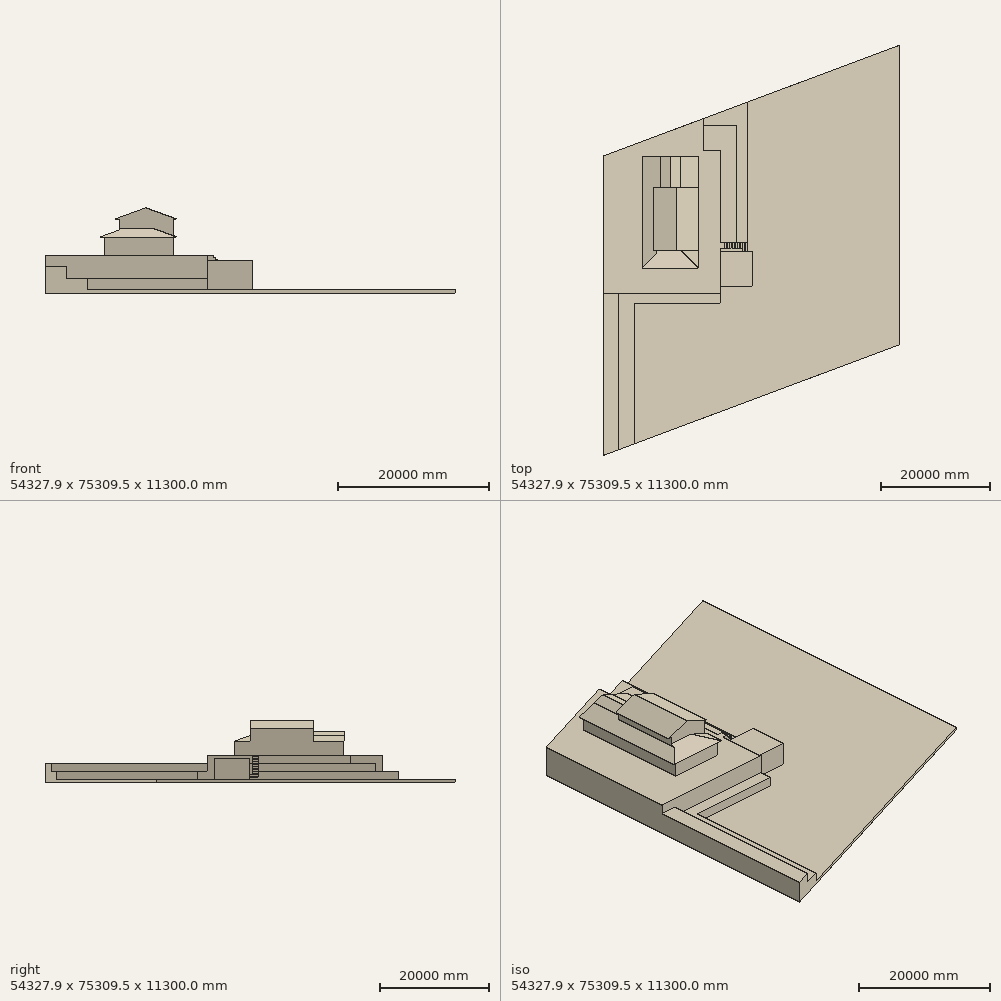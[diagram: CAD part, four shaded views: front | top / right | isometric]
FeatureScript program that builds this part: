
annotation { "Feature Type Name" : "Feature", "Feature Type Description" : "" }
export const myFeature = defineFeature(function(context is Context, id is Id, definition is map)
    precondition{}
    {
        {
            var Q0;
            Q0=qCreatedBy(makeId("Top.planeOp"),FACE);
            var sketch = newSketch(context, id + "F0", { "sketchPlane" : qUnion([Q0])});
            skLineSegment(sketch, "E0.bottom", {"start": v(0, 0) * mm, "end": v(-9140, 0) * mm});
            skLineSegment(sketch, "E0.top", {"start": v(0, 20000) * mm, "end": v(-9140, 20000) * mm});
            skLineSegment(sketch, "E0.left", {"start": v(0, 0) * mm, "end": v(0, 20000) * mm});
            skLineSegment(sketch, "E0.right", {"start": v(-9140, 0) * mm, "end": v(-9140, 20000) * mm});
            skSolve(sketch);
        }
        {
            var Q0;
            Q0 = qSketchRegion(id + "F0", true);
            extrude(context, id + "F1", {"entities" : qUnion([Q0]), "depth" : 2400 * mm, "offsetDistance" : 25 * mm});
        }
        {
            var Q0;
            Q0=makeQuery(id+"F1.opExtrude","CAP_FACE",FACE,{"disambiguationData":[OSD([sQuery(id+"F0.wireOp",EDGE,"E0.bottom"),sQuery(id+"F0.wireOp",EDGE,"E0.top"),sQuery(id+"F0.wireOp",EDGE,"E0.left"),sQuery(id+"F0.wireOp",EDGE,"E0.right")])],"isStart":false});
            var sketch = newSketch(context, id + "F2", { "sketchPlane" : qUnion([Q0])});
            skLineSegment(sketch, "E1", {"start": v(0, 0) * mm, "end": v(0, 3000) * mm});
            skLineSegment(sketch, "E2", {"start": v(0, 3000) * mm, "end": v(-7140, 3000) * mm});
            skLineSegment(sketch, "E3", {"start": v(-7140, 3000) * mm, "end": v(-7140, 14500) * mm});
            skLineSegment(sketch, "E4", {"start": v(-7140, 14500) * mm, "end": v(0, 14500) * mm});
            skLineSegment(sketch, "E5", {"start": v(0, 14500) * mm, "end": v(0, 3000) * mm});
            skSolve(sketch);
        }
        {
            var Q0;
            Q0 = qSketchRegion(id + "F2", true);
            extrude(context, id + "F3", {"entities" : qUnion([Q0]), "operationType" : NewBodyOperationType.ADD, "depth" : 2400 * mm, "offsetDistance" : 25 * mm});
        }
        {
            var Q0;
            Q0=makeQuery(id+"F3.opExtrude","CAP_FACE",FACE,{"disambiguationData":[OSD([sQuery(id+"F2.wireOp",EDGE,"E2"),sQuery(id+"F2.wireOp",EDGE,"E3"),sQuery(id+"F2.wireOp",EDGE,"E4"),sQuery(id+"F2.wireOp",EDGE,"E5")])],"isStart":false});
            var sketch = newSketch(context, id + "F4", { "sketchPlane" : qUnion([Q0])});
            skLineSegment(sketch, "E6", {"start": v(-3570, 3000) * mm, "end": v(-7740, 3000) * mm});
            skLineSegment(sketch, "E7", {"start": v(-7740, 3000) * mm, "end": v(-7740, 14500) * mm});
            skLineSegment(sketch, "E8", {"start": v(-7740, 14500) * mm, "end": v(600, 14500) * mm});
            skLineSegment(sketch, "E9", {"start": v(600, 14500) * mm, "end": v(600, 3000) * mm});
            skLineSegment(sketch, "E10", {"start": v(600, 3000) * mm, "end": v(-3570, 3000) * mm});
            skSolve(sketch);
        }
        {
            var Q0;
            Q0 = qSketchRegion(id + "F4", true);
            extrude(context, id + "F5", {"entities" : qUnion([Q0]), "operationType" : NewBodyOperationType.ADD, "depth" : 1500 * mm, "offsetDistance" : 25 * mm});
        }
        {
            var Q0;
            Q0=makeQuery(id+"F5.opExtrude","CAP_EDGE",EDGE,{"disambiguationData":[OSD([sQuery(id+"F4.wireOp",EDGE,"E9")])],"isStart":false});
            var Q1;
            Q1=makeQuery(id+"F5.opExtrude","CAP_EDGE",EDGE,{"disambiguationData":[OSD([sQuery(id+"F4.wireOp",EDGE,"E7")])],"isStart":false});
            chamfer(context, id + "F6", {"entities" : qUnion([Q0, Q1]), "chamferType" : ChamferType.OFFSET_ANGLE, "width" : 4170 * mm, "oppositeDirection" : true, "angle" : 20 * degree, "tangentPropagation" : true});
        }
        {
            var Q0;
            Q0=makeQuery(id+"F1.opExtrude","CAP_FACE",FACE,{"disambiguationData":[OSD([sQuery(id+"F0.wireOp",EDGE,"E0.bottom"),sQuery(id+"F0.wireOp",EDGE,"E0.top"),sQuery(id+"F0.wireOp",EDGE,"E0.left"),sQuery(id+"F0.wireOp",EDGE,"E0.right")])],"isStart":false});
            var sketch = newSketch(context, id + "F7", { "sketchPlane" : qUnion([Q0])});
            skLineSegment(sketch, "E11", {"start": v(0, 3000) * mm, "end": v(-7140, 3000) * mm});
            skLineSegment(sketch, "E12", {"start": v(-9740, 3000) * mm, "end": v(-9740, -300) * mm});
            skLineSegment(sketch, "E13", {"start": v(-9740, -300) * mm, "end": v(600, -300) * mm});
            skLineSegment(sketch, "E14", {"start": v(600, -300) * mm, "end": v(600, 3000) * mm});
            skLineSegment(sketch, "E15", {"start": v(600, 3000) * mm, "end": v(0, 3000) * mm});
            skPoint(sketch, "E16.start.orphan", {"position": v(600, 14500) * mm});
            skLineSegment(sketch, "E17", {"start": v(-7140, 3000) * mm, "end": v(-7140, 14500) * mm});
            skLineSegment(sketch, "E18", {"start": v(-7140, 14500) * mm, "end": v(600, 14500) * mm});
            skLineSegment(sketch, "E19", {"start": v(600, 14500) * mm, "end": v(600, 20300) * mm});
            skLineSegment(sketch, "E20", {"start": v(600, 20300) * mm, "end": v(-9740, 20300) * mm});
            skLineSegment(sketch, "E21", {"start": v(-9740, 20300) * mm, "end": v(-9740, 3000) * mm});
            skSolve(sketch);
        }
        {
            var Q0;
            Q0 = qSketchRegion(id + "F7", true);
            extrude(context, id + "F8", {"entities" : qUnion([Q0]), "operationType" : NewBodyOperationType.ADD, "depth" : 1200 * mm, "offsetDistance" : 25 * mm});
        }
        {
            var Q0;
            Q0=makeQuery(id+"F8.opExtrude","CAP_EDGE",EDGE,{"disambiguationData":[OSD([sQuery(id+"F7.wireOp",EDGE,"E13")])],"isStart":false});
            var Q1;
            Q1=makeQuery(id+"F8.opExtrude","CAP_EDGE",EDGE,{"disambiguationData":[OSD([sQuery(id+"F7.wireOp",EDGE,"E14")])],"isStart":false});
            chamfer(context, id + "F9", {"entities" : qUnion([Q0, Q1]), "chamferType" : ChamferType.OFFSET_ANGLE, "width" : 3300 * mm, "oppositeDirection" : false, "angle" : 20 * degree, "tangentPropagation" : true});
        }
        {
            var Q0;
            Q0=makeQuery(id+"F8.opExtrude","CAP_EDGE",EDGE,{"disambiguationData":[OSD([sQuery(id+"F7.wireOp",EDGE,"E19")])],"isStart":false});
            var Q1;
            Q1=makeQuery(id+"F8.opExtrude","CAP_EDGE",EDGE,{"disambiguationData":[OSD([sQuery(id+"F7.wireOp",EDGE,"E12"),sQuery(id+"F7.wireOp",EDGE,"E21")])],"isStart":false});
            chamfer(context, id + "F10", {"entities" : qUnion([Q0, Q1]), "chamferType" : ChamferType.OFFSET_ANGLE, "width" : 3300 * mm, "oppositeDirection" : false, "angle" : 20 * degree, "tangentPropagation" : true});
        }
        {
            var Q0;
            Q0=makeQuery(id+"F8.opExtrude","CAP_FACE",FACE,{"disambiguationData":[OSD([sQuery(id+"F7.wireOp",EDGE,"E11"),sQuery(id+"F7.wireOp",EDGE,"E12"),sQuery(id+"F7.wireOp",EDGE,"E13"),sQuery(id+"F7.wireOp",EDGE,"E14"),sQuery(id+"F7.wireOp",EDGE,"E15"),sQuery(id+"F7.wireOp",EDGE,"E17"),sQuery(id+"F7.wireOp",EDGE,"E18"),sQuery(id+"F7.wireOp",EDGE,"E19"),sQuery(id+"F7.wireOp",EDGE,"E20"),sQuery(id+"F7.wireOp",EDGE,"E21")])],"isStart":false});
            extrude(context, id + "F11", {"entities" : qUnion([Q0]), "operationType" : NewBodyOperationType.ADD, "depth" : 700 * mm, "offsetDistance" : 25 * mm});
        }
        {
            var Q0;
            {var subQ0=sQuery(id+"F7.wireOp",EDGE,"E21");var subQ1=sQuery(id+"F7.wireOp",EDGE,"E20");var subQ2=sQuery(id+"F7.wireOp",EDGE,"E19");var subQ3=sQuery(id+"F7.wireOp",EDGE,"E18");var subQ4=sQuery(id+"F7.wireOp",EDGE,"E17");var subQ5=sQuery(id+"F7.wireOp",EDGE,"E15");var subQ6=sQuery(id+"F7.wireOp",EDGE,"E14");var subQ7=sQuery(id+"F7.wireOp",EDGE,"E13");var subQ8=sQuery(id+"F7.wireOp",EDGE,"E12");var subQ9=sQuery(id+"F7.wireOp",EDGE,"E11");Q0=makeQuery(id+"F11.opExtrude","CAP_EDGE",EDGE,{"disambiguationData":[OSD([subQ9,subQ8,subQ7,subQ6,subQ5,subQ4,subQ3,subQ2,subQ1,subQ0]),TDD([makeQuery(id+"F10.opChamfer","BLEND_EDGE",EDGE,{"blendedFrom":[makeQuery(id+"F8.opExtrude","CAP_EDGE",EDGE,{"disambiguationData":[OSD([subQ8,subQ0])],"isStart":false}),makeQuery(id+"F8.opExtrude","CAP_FACE",FACE,{"disambiguationData":[OSD([subQ9,subQ8,subQ7,subQ6,subQ5,subQ4,subQ3,subQ2,subQ1,subQ0])],"isStart":false})],"blendedInto":[makeQuery(id+"F8.opExtrude","CAP_FACE",FACE,{"disambiguationData":[OSD([subQ9,subQ8,subQ7,subQ6,subQ5,subQ4,subQ3,subQ2,subQ1,subQ0])],"isStart":false})]})])],"isStart":false});}
            var Q1;
            {var subQ0=sQuery(id+"F7.wireOp",EDGE,"E21");var subQ1=sQuery(id+"F7.wireOp",EDGE,"E20");var subQ2=sQuery(id+"F7.wireOp",EDGE,"E19");var subQ3=sQuery(id+"F7.wireOp",EDGE,"E18");var subQ4=sQuery(id+"F7.wireOp",EDGE,"E17");var subQ5=sQuery(id+"F7.wireOp",EDGE,"E15");var subQ6=sQuery(id+"F7.wireOp",EDGE,"E14");var subQ7=sQuery(id+"F7.wireOp",EDGE,"E13");var subQ8=sQuery(id+"F7.wireOp",EDGE,"E12");var subQ9=sQuery(id+"F7.wireOp",EDGE,"E11");Q1=makeQuery(id+"F11.opExtrude","CAP_EDGE",EDGE,{"disambiguationData":[OSD([subQ9,subQ8,subQ7,subQ6,subQ5,subQ4,subQ3,subQ2,subQ1,subQ0]),TDD([makeQuery(id+"F10.opChamfer","BLEND_EDGE",EDGE,{"blendedFrom":[makeQuery(id+"F8.opExtrude","CAP_EDGE",EDGE,{"disambiguationData":[OSD([subQ2])],"isStart":false}),makeQuery(id+"F8.opExtrude","CAP_FACE",FACE,{"disambiguationData":[OSD([subQ9,subQ8,subQ7,subQ6,subQ5,subQ4,subQ3,subQ2,subQ1,subQ0])],"isStart":false})],"blendedInto":[makeQuery(id+"F8.opExtrude","CAP_FACE",FACE,{"disambiguationData":[OSD([subQ9,subQ8,subQ7,subQ6,subQ5,subQ4,subQ3,subQ2,subQ1,subQ0])],"isStart":false})]})])],"isStart":false});}
            chamfer(context, id + "F12", {"entities" : qUnion([Q0, Q1]), "chamferType" : ChamferType.OFFSET_ANGLE, "width" : 1923.2 * mm, "oppositeDirection" : false, "angle" : 20 * degree, "tangentPropagation" : true});
        }
        {
            var Q0;
            Q0=makeQuery(id+"F1.opExtrude","CAP_FACE",FACE,{"disambiguationData":[OSD([sQuery(id+"F0.wireOp",EDGE,"E0.bottom"),sQuery(id+"F0.wireOp",EDGE,"E0.top"),sQuery(id+"F0.wireOp",EDGE,"E0.left"),sQuery(id+"F0.wireOp",EDGE,"E0.right")])],"isStart":true});
            var sketch = newSketch(context, id + "F13", { "sketchPlane" : qUnion([Q0])});
            skLineSegment(sketch, "E22", {"start": v(0, 0) * mm, "end": v(0, 3700) * mm});
            skLineSegment(sketch, "E23", {"start": v(0, 3700) * mm, "end": v(4500, 3700) * mm});
            skLineSegment(sketch, "E24", {"start": v(4500, 3700) * mm, "end": v(4500, -28300) * mm});
            skLineSegment(sketch, "E25", {"start": v(0, 3700) * mm, "end": v(-16900, 3700) * mm});
            skLineSegment(sketch, "E26", {"start": v(-16900, 3700) * mm, "end": v(-16900, -20300) * mm});
            skLineSegment(sketch, "E27", {"start": v(-16900, -20300) * mm, "end": v(4500, -28300) * mm});
            skSolve(sketch);
        }
        {
            var Q0;
            Q0 = qSketchRegion(id + "F13", true);
            extrude(context, id + "F14", {"entities" : qUnion([Q0]), "operationType" : NewBodyOperationType.ADD, "depth" : 200 * mm, "offsetDistance" : 25 * mm});
        }
        {
            var Q0;
            Q0=makeQuery(id+"F14.opExtrude","CAP_FACE",FACE,{"disambiguationData":[OSD([sQuery(id+"F13.wireOp",EDGE,"E23"),sQuery(id+"F13.wireOp",EDGE,"E24"),sQuery(id+"F13.wireOp",EDGE,"E25"),sQuery(id+"F13.wireOp",EDGE,"E26"),sQuery(id+"F13.wireOp",EDGE,"E27")])],"isStart":false});
            var sketch = newSketch(context, id + "F15", { "sketchPlane" : qUnion([Q0])});
            skLineSegment(sketch, "E28", {"start": v(-16900, -20300) * mm, "end": v(37427.93, -40609.5) * mm});
            skLineSegment(sketch, "E29", {"start": v(37427.93, -40609.5) * mm, "end": v(37427.93, 14390.5) * mm});
            skLineSegment(sketch, "E30", {"start": v(37427.93, 14390.5) * mm, "end": v(-16900, 34700) * mm});
            skLineSegment(sketch, "E31", {"start": v(-16900, 34700) * mm, "end": v(-16900, -20300) * mm});
            skSolve(sketch);
        }
        {
            var Q0;
            Q0 = qSketchRegion(id + "F15", true);
            extrude(context, id + "F16", {"entities" : qUnion([Q0]), "operationType" : NewBodyOperationType.ADD, "depth" : 4800 * mm, "offsetDistance" : 25 * mm});
        }
        {
            var Q0;
            Q0=makeQuery(id+"F16.opExtrude","CAP_FACE",FACE,{"disambiguationData":[OSD([sQuery(id+"F15.wireOp",EDGE,"E28"),sQuery(id+"F15.wireOp",EDGE,"E29"),sQuery(id+"F15.wireOp",EDGE,"E30"),sQuery(id+"F15.wireOp",EDGE,"E31")])],"isStart":true});
            extrude(context, id + "F17", {"entities" : qUnion([Q0]), "operationType" : NewBodyOperationType.ADD, "depth" : 25 * mm, "offsetDistance" : 25 * mm});
        }
        {
            var Q0;
            Q0=makeQuery(id+"F17.opExtrude","CAP_FACE",FACE,{"disambiguationData":[OSD([sQuery(id+"F15.wireOp",EDGE,"E28"),sQuery(id+"F15.wireOp",EDGE,"E29"),sQuery(id+"F15.wireOp",EDGE,"E30"),sQuery(id+"F15.wireOp",EDGE,"E31")])],"isStart":false});
            var sketch = newSketch(context, id + "F18", { "sketchPlane" : qUnion([Q0])});
            skLineSegment(sketch, "E32", {"start": v(-16900, -3700) * mm, "end": v(4500, -3700) * mm});
            skLineSegment(sketch, "E33", {"start": v(4500, -3700) * mm, "end": v(4500, 28300) * mm});
            skLineSegment(sketch, "E34", {"start": v(4500, 28300) * mm, "end": v(37427.93, 40609.5) * mm});
            skLineSegment(sketch, "E35", {"start": v(37427.93, 40609.5) * mm, "end": v(37427.93, -14390.5) * mm});
            skLineSegment(sketch, "E36", {"start": v(37427.93, -14390.5) * mm, "end": v(-16900, -34700) * mm});
            skLineSegment(sketch, "E37", {"start": v(-16900, -34700) * mm, "end": v(-16900, -3700) * mm});
            skSolve(sketch);
        }
        {
            var Q0;
            Q0 = qSketchRegion(id + "F18", true);
            extrude(context, id + "F19", {"entities" : qUnion([Q0]), "operationType" : NewBodyOperationType.REMOVE, "oppositeDirection" : true, "depth" : 1325 * mm, "offsetDistance" : 25 * mm});
        }
        {
            var Q0;
            Q0=makeQuery(id+"F14.opExtrude","CAP_FACE",FACE,{"disambiguationData":[OSD([sQuery(id+"F13.wireOp",EDGE,"E23"),sQuery(id+"F13.wireOp",EDGE,"E24"),sQuery(id+"F13.wireOp",EDGE,"E25"),sQuery(id+"F13.wireOp",EDGE,"E26"),sQuery(id+"F13.wireOp",EDGE,"E27")])],"isStart":true});
            var sketch = newSketch(context, id + "F20", { "sketchPlane" : qUnion([Q0])});
            skLineSegment(sketch, "E38", {"start": v(4500, 28300) * mm, "end": v(4500, 21300) * mm});
            skLineSegment(sketch, "E39", {"start": v(4500, 21300) * mm, "end": v(1500, 21300) * mm});
            skLineSegment(sketch, "E40", {"start": v(1500, 21300) * mm, "end": v(1500, 27178.5) * mm});
            skLineSegment(sketch, "E41", {"start": v(1500, 27178.5) * mm, "end": v(4500, 28300) * mm});
            skSolve(sketch);
        }
        {
            var Q0;
            Q0 = qSketchRegion(id + "F20", true);
            extrude(context, id + "F21", {"entities" : qUnion([Q0]), "operationType" : NewBodyOperationType.REMOVE, "oppositeDirection" : true, "depth" : 1500 * mm, "offsetDistance" : 25 * mm});
        }
        {
            var Q0;
            Q0=makeQuery(id+"F21.boolean.opBoolean","MERGE",FACE,{"derivedFrom":[makeQuery(id+"F19.boolean.opBoolean","COPY",FACE,{"derivedFrom":makeQuery(id+"F19.opExtrude","CAP_FACE",FACE,{"disambiguationData":[OSD([sQuery(id+"F18.wireOp",EDGE,"E32"),sQuery(id+"F18.wireOp",EDGE,"E33"),sQuery(id+"F18.wireOp",EDGE,"E34"),sQuery(id+"F18.wireOp",EDGE,"E35"),sQuery(id+"F18.wireOp",EDGE,"E36"),sQuery(id+"F18.wireOp",EDGE,"E37")])],"isStart":false})})],"fromTools":[makeQuery(id+"F21.opExtrude","CAP_FACE",FACE,{"disambiguationData":[OSD([sQuery(id+"F20.wireOp",EDGE,"E38"),sQuery(id+"F20.wireOp",EDGE,"E39"),sQuery(id+"F20.wireOp",EDGE,"E40"),sQuery(id+"F20.wireOp",EDGE,"E41")])],"isStart":false})]});
            var sketch = newSketch(context, id + "F22", { "sketchPlane" : qUnion([Q0])});
            skLineSegment(sketch, "E42", {"start": v(4500, -3700) * mm, "end": v(4500, 4440) * mm});
            skLineSegment(sketch, "E43", {"start": v(4500, 4440) * mm, "end": v(7500, 4440) * mm});
            skLineSegment(sketch, "E44", {"start": v(7500, 4440) * mm, "end": v(7500, 25900) * mm});
            skLineSegment(sketch, "E45", {"start": v(7500, 25900) * mm, "end": v(1500, 25900) * mm});
            skLineSegment(sketch, "E46", {"start": v(1500, 25900) * mm, "end": v(1500, 27178.5) * mm});
            skLineSegment(sketch, "E47", {"start": v(1500, 27178.5) * mm, "end": v(37427.93, 40609.5) * mm});
            skLineSegment(sketch, "E48", {"start": v(37427.93, 40609.5) * mm, "end": v(37427.93, -14390.5) * mm});
            skLineSegment(sketch, "E49", {"start": v(37427.93, -14390.5) * mm, "end": v(-14089.93, -33649.5) * mm});
            skLineSegment(sketch, "E50", {"start": v(-14089.93, -33649.5) * mm, "end": v(-14089.93, -3700) * mm});
            skLineSegment(sketch, "E51", {"start": v(-14089.93, -3700) * mm, "end": v(4500, -3700) * mm});
            skSolve(sketch);
        }
        {
            var Q0;
            Q0 = qSketchRegion(id + "F22", true);
            extrude(context, id + "F23", {"entities" : qUnion([Q0]), "operationType" : NewBodyOperationType.REMOVE, "oppositeDirection" : true, "depth" : 1500 * mm, "offsetDistance" : 25 * mm});
        }
        {
            var Q0;
            Q0=makeQuery(id+"F23.boolean.opBoolean","COPY",FACE,{"derivedFrom":makeQuery(id+"F23.opExtrude","CAP_FACE",FACE,{"disambiguationData":[OSD([sQuery(id+"F22.wireOp",EDGE,"E42"),sQuery(id+"F22.wireOp",EDGE,"E43"),sQuery(id+"F22.wireOp",EDGE,"E44"),sQuery(id+"F22.wireOp",EDGE,"E45"),sQuery(id+"F22.wireOp",EDGE,"E46"),sQuery(id+"F22.wireOp",EDGE,"E47"),sQuery(id+"F22.wireOp",EDGE,"E48"),sQuery(id+"F22.wireOp",EDGE,"E49"),sQuery(id+"F22.wireOp",EDGE,"E50"),sQuery(id+"F22.wireOp",EDGE,"E51")])],"isStart":false})});
            var sketch = newSketch(context, id + "F24", { "sketchPlane" : qUnion([Q0])});
            skLineSegment(sketch, "E52", {"start": v(4500, -3700) * mm, "end": v(4500, 4440) * mm});
            skLineSegment(sketch, "E53", {"start": v(4500, 4440) * mm, "end": v(9500, 4440) * mm});
            skLineSegment(sketch, "E54", {"start": v(9500, 4440) * mm, "end": v(9500, 30169.16) * mm});
            skLineSegment(sketch, "E55", {"start": v(9500, 30169.16) * mm, "end": v(37427.93, 40609.5) * mm});
            skLineSegment(sketch, "E56", {"start": v(37427.93, 40609.5) * mm, "end": v(37427.93, -14390.5) * mm});
            skLineSegment(sketch, "E57", {"start": v(37427.93, -14390.5) * mm, "end": v(-11279.87, -32599.02) * mm});
            skLineSegment(sketch, "E58", {"start": v(-11279.87, -32599.02) * mm, "end": v(-11279.87, -5700) * mm});
            skLineSegment(sketch, "E59", {"start": v(-11279.87, -5700) * mm, "end": v(4500, -5700) * mm});
            skLineSegment(sketch, "E60", {"start": v(4500, -5700) * mm, "end": v(4500, -3700) * mm});
            skSolve(sketch);
        }
        {
            var Q0;
            Q0 = qSketchRegion(id + "F24", true);
            extrude(context, id + "F25", {"entities" : qUnion([Q0]), "operationType" : NewBodyOperationType.REMOVE, "oppositeDirection" : true, "depth" : 1500 * mm, "offsetDistance" : 25 * mm});
        }
        {
            var Q0;
            Q0=makeQuery(id+"F25.boolean.opBoolean","COPY",FACE,{"derivedFrom":makeQuery(id+"F25.opExtrude","CAP_FACE",FACE,{"disambiguationData":[OSD([sQuery(id+"F24.wireOp",EDGE,"E52"),sQuery(id+"F24.wireOp",EDGE,"E53"),sQuery(id+"F24.wireOp",EDGE,"E54"),sQuery(id+"F24.wireOp",EDGE,"E55"),sQuery(id+"F24.wireOp",EDGE,"E56"),sQuery(id+"F24.wireOp",EDGE,"E57"),sQuery(id+"F24.wireOp",EDGE,"E58"),sQuery(id+"F24.wireOp",EDGE,"E59"),sQuery(id+"F24.wireOp",EDGE,"E60")])],"isStart":false})});
            var sketch = newSketch(context, id + "F26", { "sketchPlane" : qUnion([Q0])});
            skLineSegment(sketch, "E61", {"start": v(4500, -3700) * mm, "end": v(4500, 3300) * mm});
            skLineSegment(sketch, "E62", {"start": v(4500, 3300) * mm, "end": v(10500, 3300) * mm});
            skLineSegment(sketch, "E63", {"start": v(10500, 3300) * mm, "end": v(10500, -3700) * mm});
            skLineSegment(sketch, "E64", {"start": v(10500, -3700) * mm, "end": v(4500, -3700) * mm});
            skSolve(sketch);
        }
        {
            var Q0;
            Q0 = qSketchRegion(id + "F26", true);
            extrude(context, id + "F27", {"entities" : qUnion([Q0]), "operationType" : NewBodyOperationType.ADD, "depth" : 3800 * mm, "offsetDistance" : 25 * mm});
        }
        {
            var Q0;
            Q0=makeQuery(id+"F25.boolean.opBoolean","COPY",FACE,{"derivedFrom":makeQuery(id+"F25.opExtrude","CAP_FACE",FACE,{"disambiguationData":[OSD([sQuery(id+"F24.wireOp",EDGE,"E52"),sQuery(id+"F24.wireOp",EDGE,"E53"),sQuery(id+"F24.wireOp",EDGE,"E54"),sQuery(id+"F24.wireOp",EDGE,"E55"),sQuery(id+"F24.wireOp",EDGE,"E56"),sQuery(id+"F24.wireOp",EDGE,"E57"),sQuery(id+"F24.wireOp",EDGE,"E58"),sQuery(id+"F24.wireOp",EDGE,"E59"),sQuery(id+"F24.wireOp",EDGE,"E60")])],"isStart":false})});
            var sketch = newSketch(context, id + "F28", { "sketchPlane" : qUnion([Q0])});
            skLineSegment(sketch, "E65", {"start": v(9500, 4440) * mm, "end": v(9500, 3300) * mm});
            skLineSegment(sketch, "E66", {"start": v(9500, 3300) * mm, "end": v(4500, 3300) * mm});
            skLineSegment(sketch, "E67", {"start": v(4500, 3300) * mm, "end": v(4500, 4440) * mm});
            skLineSegment(sketch, "E68", {"start": v(4500, 4440) * mm, "end": v(9500, 4440) * mm});
            skSolve(sketch);
        }
        {
            var Q0;
            Q0 = qSketchRegion(id + "F28", true);
            extrude(context, id + "F29", {"entities" : qUnion([Q0]), "operationType" : NewBodyOperationType.ADD, "depth" : 300 * mm, "offsetDistance" : 25 * mm});
        }
        {
            var Q0;
            Q0=makeQuery(id+"F29.opExtrude","CAP_FACE",FACE,{"disambiguationData":[OSD([sQuery(id+"F28.wireOp",EDGE,"E65"),sQuery(id+"F28.wireOp",EDGE,"E66"),sQuery(id+"F28.wireOp",EDGE,"E67"),sQuery(id+"F28.wireOp",EDGE,"E68")])],"isStart":false});
            var sketch = newSketch(context, id + "F30", { "sketchPlane" : qUnion([Q0])});
            skLineSegment(sketch, "E69", {"start": v(4500, 4440) * mm, "end": v(9200, 4440) * mm});
            skLineSegment(sketch, "E70", {"start": v(9200, 4440) * mm, "end": v(9200, 3300) * mm});
            skLineSegment(sketch, "E71", {"start": v(9200, 3300) * mm, "end": v(4500, 3300) * mm});
            skLineSegment(sketch, "E72", {"start": v(4500, 3300) * mm, "end": v(4500, 4351.93) * mm});
            skLineSegment(sketch, "E73", {"start": v(4500, 4351.93) * mm, "end": v(4500, 4440) * mm});
            skSolve(sketch);
        }
        {
            var Q0;
            Q0 = qSketchRegion(id + "F30", true);
            extrude(context, id + "F31", {"entities" : qUnion([Q0]), "operationType" : NewBodyOperationType.ADD, "depth" : 300 * mm, "offsetDistance" : 25 * mm});
        }
        {
            var Q0;
            Q0=makeQuery(id+"F31.opExtrude","CAP_FACE",FACE,{"disambiguationData":[OSD([sQuery(id+"F30.wireOp",EDGE,"E69"),sQuery(id+"F30.wireOp",EDGE,"E70"),sQuery(id+"F30.wireOp",EDGE,"E71"),sQuery(id+"F30.wireOp",EDGE,"E72"),sQuery(id+"F30.wireOp",EDGE,"E73")])],"isStart":false});
            var sketch = newSketch(context, id + "F32", { "sketchPlane" : qUnion([Q0])});
            skLineSegment(sketch, "E74.bottom", {"start": v(4500, 4440) * mm, "end": v(8900, 4440) * mm});
            skLineSegment(sketch, "E74.top", {"start": v(4500, 3300) * mm, "end": v(8900, 3300) * mm});
            skLineSegment(sketch, "E74.left", {"start": v(4500, 4440) * mm, "end": v(4500, 3300) * mm});
            skLineSegment(sketch, "E74.right", {"start": v(8900, 4440) * mm, "end": v(8900, 3300) * mm});
            skSolve(sketch);
        }
        {
            var Q0;
            Q0 = qSketchRegion(id + "F32", true);
            extrude(context, id + "F33", {"entities" : qUnion([Q0]), "operationType" : NewBodyOperationType.ADD, "depth" : 300 * mm, "offsetDistance" : 25 * mm});
        }
        {
            var Q0;
            Q0=makeQuery(id+"F33.opExtrude","CAP_FACE",FACE,{"disambiguationData":[OSD([sQuery(id+"F32.wireOp",EDGE,"E74.bottom"),sQuery(id+"F32.wireOp",EDGE,"E74.top"),sQuery(id+"F32.wireOp",EDGE,"E74.left"),sQuery(id+"F32.wireOp",EDGE,"E74.right")])],"isStart":false});
            var sketch = newSketch(context, id + "F34", { "sketchPlane" : qUnion([Q0])});
            skLineSegment(sketch, "E75.bottom", {"start": v(4500, 4440) * mm, "end": v(8600, 4440) * mm});
            skLineSegment(sketch, "E75.top", {"start": v(4500, 3300) * mm, "end": v(8600, 3300) * mm});
            skLineSegment(sketch, "E75.left", {"start": v(4500, 4440) * mm, "end": v(4500, 3300) * mm});
            skLineSegment(sketch, "E75.right", {"start": v(8600, 4440) * mm, "end": v(8600, 3300) * mm});
            skSolve(sketch);
        }
        {
            var Q0;
            Q0 = qSketchRegion(id + "F34", true);
            extrude(context, id + "F35", {"entities" : qUnion([Q0]), "operationType" : NewBodyOperationType.ADD, "depth" : 300 * mm, "offsetDistance" : 25 * mm});
        }
        {
            var Q0;
            Q0=makeQuery(id+"F35.opExtrude","CAP_FACE",FACE,{"disambiguationData":[OSD([sQuery(id+"F34.wireOp",EDGE,"E75.bottom"),sQuery(id+"F34.wireOp",EDGE,"E75.top"),sQuery(id+"F34.wireOp",EDGE,"E75.left"),sQuery(id+"F34.wireOp",EDGE,"E75.right")])],"isStart":false});
            var sketch = newSketch(context, id + "F36", { "sketchPlane" : qUnion([Q0])});
            skLineSegment(sketch, "E76.bottom", {"start": v(4500, 4440) * mm, "end": v(8300, 4440) * mm});
            skLineSegment(sketch, "E76.top", {"start": v(4500, 3300) * mm, "end": v(8300, 3300) * mm});
            skLineSegment(sketch, "E76.left", {"start": v(4500, 4440) * mm, "end": v(4500, 3300) * mm});
            skLineSegment(sketch, "E76.right", {"start": v(8300, 4440) * mm, "end": v(8300, 3300) * mm});
            skSolve(sketch);
        }
        {
            var Q0;
            Q0 = qSketchRegion(id + "F36", true);
            extrude(context, id + "F37", {"entities" : qUnion([Q0]), "operationType" : NewBodyOperationType.ADD, "depth" : 300 * mm, "offsetDistance" : 25 * mm});
        }
        {
            var Q0;
            {var subQ1=sQuery(id+"F22.wireOp",EDGE,"E45");var subQ2=sQuery(id+"F22.wireOp",EDGE,"E43");var subQ3=sQuery(id+"F22.wireOp",EDGE,"E44");Q0=makeQuery(id+"F37.boolean.opBoolean","MERGE",FACE,{"derivedFrom":[makeQuery(id+"F25.boolean.opBoolean","SPLIT",FACE,{"disambiguationData":[TD([makeQuery(id+"F14.opExtrude","SWEPT_FACE",FACE,{"disambiguationData":[OSD([sQuery(id+"F13.wireOp",EDGE,"E27")])]})])],"derivedFrom":makeQuery(id+"F23.boolean.opBoolean","COPY",FACE,{"derivedFrom":makeQuery(id+"F23.opExtrude","CAP_FACE",FACE,{"disambiguationData":[OSD([sQuery(id+"F22.wireOp",EDGE,"E42"),subQ2,subQ3,subQ1,sQuery(id+"F22.wireOp",EDGE,"E46"),sQuery(id+"F22.wireOp",EDGE,"E47"),sQuery(id+"F22.wireOp",EDGE,"E48"),sQuery(id+"F22.wireOp",EDGE,"E49"),sQuery(id+"F22.wireOp",EDGE,"E50"),sQuery(id+"F22.wireOp",EDGE,"E51")])],"isStart":false})})}),makeQuery(id+"F37.opExtrude","CAP_FACE",FACE,{"disambiguationData":[OSD([sQuery(id+"F36.wireOp",EDGE,"E76.bottom"),sQuery(id+"F36.wireOp",EDGE,"E76.top"),sQuery(id+"F36.wireOp",EDGE,"E76.left"),sQuery(id+"F36.wireOp",EDGE,"E76.right")])],"isStart":false})]});}
            var sketch = newSketch(context, id + "F38", { "sketchPlane" : qUnion([Q0])});
            skLineSegment(sketch, "E77.bottom", {"start": v(4500, 4440) * mm, "end": v(8000, 4440) * mm});
            skLineSegment(sketch, "E77.top", {"start": v(4500, 3300) * mm, "end": v(8000, 3300) * mm});
            skLineSegment(sketch, "E77.left", {"start": v(4500, 4440) * mm, "end": v(4500, 3300) * mm});
            skLineSegment(sketch, "E77.right", {"start": v(8000, 4440) * mm, "end": v(8000, 3300) * mm});
            skSolve(sketch);
        }
        {
            var Q0;
            Q0 = qSketchRegion(id + "F38", true);
            extrude(context, id + "F39", {"entities" : qUnion([Q0]), "operationType" : NewBodyOperationType.ADD, "depth" : 300 * mm, "offsetDistance" : 25 * mm});
        }
        {
            var Q0;
            Q0=makeQuery(id+"F39.opExtrude","CAP_FACE",FACE,{"disambiguationData":[OSD([sQuery(id+"F38.wireOp",EDGE,"E77.bottom"),sQuery(id+"F38.wireOp",EDGE,"E77.top"),sQuery(id+"F38.wireOp",EDGE,"E77.left"),sQuery(id+"F38.wireOp",EDGE,"E77.right")])],"isStart":false});
            var sketch = newSketch(context, id + "F40", { "sketchPlane" : qUnion([Q0])});
            skLineSegment(sketch, "E78.bottom", {"start": v(4500, 4440) * mm, "end": v(7700, 4440) * mm});
            skLineSegment(sketch, "E78.top", {"start": v(4500, 3300) * mm, "end": v(7700, 3300) * mm});
            skLineSegment(sketch, "E78.left", {"start": v(4500, 4440) * mm, "end": v(4500, 3300) * mm});
            skLineSegment(sketch, "E78.right", {"start": v(7700, 4440) * mm, "end": v(7700, 3300) * mm});
            skSolve(sketch);
        }
        {
            var Q0;
            Q0 = qSketchRegion(id + "F40", true);
            extrude(context, id + "F41", {"entities" : qUnion([Q0]), "operationType" : NewBodyOperationType.ADD, "depth" : 300 * mm, "offsetDistance" : 25 * mm});
        }
        {
            var Q0;
            Q0=makeQuery(id+"F41.opExtrude","CAP_FACE",FACE,{"disambiguationData":[OSD([sQuery(id+"F40.wireOp",EDGE,"E78.bottom"),sQuery(id+"F40.wireOp",EDGE,"E78.top"),sQuery(id+"F40.wireOp",EDGE,"E78.left"),sQuery(id+"F40.wireOp",EDGE,"E78.right")])],"isStart":false});
            var sketch = newSketch(context, id + "F42", { "sketchPlane" : qUnion([Q0])});
            skLineSegment(sketch, "E79.bottom", {"start": v(4500, 4440) * mm, "end": v(7400, 4440) * mm});
            skLineSegment(sketch, "E79.top", {"start": v(4500, 3300) * mm, "end": v(7400, 3300) * mm});
            skLineSegment(sketch, "E79.left", {"start": v(4500, 4440) * mm, "end": v(4500, 3300) * mm});
            skLineSegment(sketch, "E79.right", {"start": v(7400, 4440) * mm, "end": v(7400, 3300) * mm});
            skSolve(sketch);
        }
        {
            var Q0;
            Q0 = qSketchRegion(id + "F42", true);
            extrude(context, id + "F43", {"entities" : qUnion([Q0]), "operationType" : NewBodyOperationType.ADD, "depth" : 300 * mm, "offsetDistance" : 25 * mm});
        }
        {
            var Q0;
            Q0=makeQuery(id+"F43.opExtrude","CAP_FACE",FACE,{"disambiguationData":[OSD([sQuery(id+"F42.wireOp",EDGE,"E79.bottom"),sQuery(id+"F42.wireOp",EDGE,"E79.top"),sQuery(id+"F42.wireOp",EDGE,"E79.left"),sQuery(id+"F42.wireOp",EDGE,"E79.right")])],"isStart":false});
            var sketch = newSketch(context, id + "F44", { "sketchPlane" : qUnion([Q0])});
            skLineSegment(sketch, "E80.bottom", {"start": v(4500, 4440) * mm, "end": v(7100, 4440) * mm});
            skLineSegment(sketch, "E80.top", {"start": v(4500, 3300) * mm, "end": v(7100, 3300) * mm});
            skLineSegment(sketch, "E80.left", {"start": v(4500, 4440) * mm, "end": v(4500, 3300) * mm});
            skLineSegment(sketch, "E80.right", {"start": v(7100, 4440) * mm, "end": v(7100, 3300) * mm});
            skSolve(sketch);
        }
        {
            var Q0;
            Q0 = qSketchRegion(id + "F44", true);
            extrude(context, id + "F45", {"entities" : qUnion([Q0]), "operationType" : NewBodyOperationType.ADD, "depth" : 300 * mm, "offsetDistance" : 25 * mm});
        }
        {
            var Q0;
            Q0=makeQuery(id+"F45.opExtrude","CAP_FACE",FACE,{"disambiguationData":[OSD([sQuery(id+"F44.wireOp",EDGE,"E80.bottom"),sQuery(id+"F44.wireOp",EDGE,"E80.top"),sQuery(id+"F44.wireOp",EDGE,"E80.left"),sQuery(id+"F44.wireOp",EDGE,"E80.right")])],"isStart":false});
            var sketch = newSketch(context, id + "F46", { "sketchPlane" : qUnion([Q0])});
            skLineSegment(sketch, "E81.bottom", {"start": v(4500, 4440) * mm, "end": v(6800, 4440) * mm});
            skLineSegment(sketch, "E81.top", {"start": v(4500, 3300) * mm, "end": v(6800, 3300) * mm});
            skLineSegment(sketch, "E81.left", {"start": v(4500, 4440) * mm, "end": v(4500, 3300) * mm});
            skLineSegment(sketch, "E81.right", {"start": v(6800, 4440) * mm, "end": v(6800, 3300) * mm});
            skSolve(sketch);
        }
        {
            var Q0;
            Q0 = qSketchRegion(id + "F46", true);
            extrude(context, id + "F47", {"entities" : qUnion([Q0]), "operationType" : NewBodyOperationType.ADD, "depth" : 300 * mm, "offsetDistance" : 25 * mm});
        }
        {
            var Q0;
            {var subQ0=sQuery(id+"F20.wireOp",EDGE,"E40");var subQ1=sQuery(id+"F20.wireOp",EDGE,"E39");Q0=makeQuery(id+"F47.boolean.opBoolean","MERGE",FACE,{"derivedFrom":[makeQuery(id+"F23.boolean.opBoolean","SPLIT",FACE,{"disambiguationData":[TD([makeQuery(id+"F14.opExtrude","SWEPT_FACE",FACE,{"disambiguationData":[OSD([sQuery(id+"F13.wireOp",EDGE,"E24")])]})])],"derivedFrom":makeQuery(id+"F21.boolean.opBoolean","MERGE",FACE,{"derivedFrom":[makeQuery(id+"F19.boolean.opBoolean","COPY",FACE,{"derivedFrom":makeQuery(id+"F19.opExtrude","CAP_FACE",FACE,{"disambiguationData":[OSD([sQuery(id+"F18.wireOp",EDGE,"E32"),sQuery(id+"F18.wireOp",EDGE,"E33"),sQuery(id+"F18.wireOp",EDGE,"E34"),sQuery(id+"F18.wireOp",EDGE,"E35"),sQuery(id+"F18.wireOp",EDGE,"E36"),sQuery(id+"F18.wireOp",EDGE,"E37")])],"isStart":false})})],"fromTools":[makeQuery(id+"F21.opExtrude","CAP_FACE",FACE,{"disambiguationData":[OSD([sQuery(id+"F20.wireOp",EDGE,"E38"),subQ1,subQ0,sQuery(id+"F20.wireOp",EDGE,"E41")])],"isStart":false})]})}),makeQuery(id+"F47.opExtrude","CAP_FACE",FACE,{"disambiguationData":[OSD([sQuery(id+"F46.wireOp",EDGE,"E81.bottom"),sQuery(id+"F46.wireOp",EDGE,"E81.top"),sQuery(id+"F46.wireOp",EDGE,"E81.left"),sQuery(id+"F46.wireOp",EDGE,"E81.right")])],"isStart":false})]});}
            var sketch = newSketch(context, id + "F48", { "sketchPlane" : qUnion([Q0])});
            skLineSegment(sketch, "E82.bottom", {"start": v(4500, 3300) * mm, "end": v(6500, 3300) * mm});
            skLineSegment(sketch, "E82.top", {"start": v(4500, 4440) * mm, "end": v(6500, 4440) * mm});
            skLineSegment(sketch, "E82.left", {"start": v(4500, 3300) * mm, "end": v(4500, 4440) * mm});
            skLineSegment(sketch, "E82.right", {"start": v(6500, 3300) * mm, "end": v(6500, 4440) * mm});
            skSolve(sketch);
        }
        {
            var Q0;
            Q0 = qSketchRegion(id + "F48", true);
            extrude(context, id + "F49", {"entities" : qUnion([Q0]), "operationType" : NewBodyOperationType.ADD, "depth" : 300 * mm, "offsetDistance" : 25 * mm});
        }
        {
            var Q0;
            Q0=makeQuery(id+"F49.opExtrude","CAP_FACE",FACE,{"disambiguationData":[OSD([sQuery(id+"F48.wireOp",EDGE,"E82.bottom"),sQuery(id+"F48.wireOp",EDGE,"E82.top"),sQuery(id+"F48.wireOp",EDGE,"E82.left"),sQuery(id+"F48.wireOp",EDGE,"E82.right")])],"isStart":false});
            var sketch = newSketch(context, id + "F50", { "sketchPlane" : qUnion([Q0])});
            skLineSegment(sketch, "E83.bottom", {"start": v(4500, 3300) * mm, "end": v(6200, 3300) * mm});
            skLineSegment(sketch, "E83.top", {"start": v(4500, 4440) * mm, "end": v(6200, 4440) * mm});
            skLineSegment(sketch, "E83.left", {"start": v(4500, 3300) * mm, "end": v(4500, 4440) * mm});
            skLineSegment(sketch, "E83.right", {"start": v(6200, 3300) * mm, "end": v(6200, 4440) * mm});
            skSolve(sketch);
        }
        {
            var Q0;
            Q0 = qSketchRegion(id + "F50", true);
            extrude(context, id + "F51", {"entities" : qUnion([Q0]), "operationType" : NewBodyOperationType.ADD, "depth" : 300 * mm, "offsetDistance" : 25 * mm});
        }
        {
            var Q0;
            Q0=makeQuery(id+"F51.opExtrude","CAP_FACE",FACE,{"disambiguationData":[OSD([sQuery(id+"F50.wireOp",EDGE,"E83.bottom"),sQuery(id+"F50.wireOp",EDGE,"E83.top"),sQuery(id+"F50.wireOp",EDGE,"E83.left"),sQuery(id+"F50.wireOp",EDGE,"E83.right")])],"isStart":false});
            var sketch = newSketch(context, id + "F52", { "sketchPlane" : qUnion([Q0])});
            skLineSegment(sketch, "E84.bottom", {"start": v(4500, 3300) * mm, "end": v(5900, 3300) * mm});
            skLineSegment(sketch, "E84.top", {"start": v(4500, 4440) * mm, "end": v(5900, 4440) * mm});
            skLineSegment(sketch, "E84.left", {"start": v(4500, 3300) * mm, "end": v(4500, 4440) * mm});
            skLineSegment(sketch, "E84.right", {"start": v(5900, 3300) * mm, "end": v(5900, 4440) * mm});
            skSolve(sketch);
        }
        {
            var Q0;
            Q0 = qSketchRegion(id + "F52", true);
            extrude(context, id + "F53", {"entities" : qUnion([Q0]), "operationType" : NewBodyOperationType.ADD, "depth" : 300 * mm, "offsetDistance" : 25 * mm});
        }
        {
            var Q0;
            Q0=makeQuery(id+"F53.opExtrude","CAP_FACE",FACE,{"disambiguationData":[OSD([sQuery(id+"F52.wireOp",EDGE,"E84.bottom"),sQuery(id+"F52.wireOp",EDGE,"E84.top"),sQuery(id+"F52.wireOp",EDGE,"E84.left"),sQuery(id+"F52.wireOp",EDGE,"E84.right")])],"isStart":false});
            var sketch = newSketch(context, id + "F54", { "sketchPlane" : qUnion([Q0])});
            skLineSegment(sketch, "E85.bottom", {"start": v(4500, 3300) * mm, "end": v(5600, 3300) * mm});
            skLineSegment(sketch, "E85.top", {"start": v(4500, 4440) * mm, "end": v(5600, 4440) * mm});
            skLineSegment(sketch, "E85.left", {"start": v(4500, 3300) * mm, "end": v(4500, 4440) * mm});
            skLineSegment(sketch, "E85.right", {"start": v(5600, 3300) * mm, "end": v(5600, 4440) * mm});
            skSolve(sketch);
        }
        {
            var Q0;
            Q0 = qSketchRegion(id + "F54", true);
            extrude(context, id + "F55", {"entities" : qUnion([Q0]), "operationType" : NewBodyOperationType.ADD, "depth" : 300 * mm, "offsetDistance" : 25 * mm});
        }
        {
            var Q0;
            Q0=makeQuery(id+"F55.opExtrude","CAP_FACE",FACE,{"disambiguationData":[OSD([sQuery(id+"F54.wireOp",EDGE,"E85.bottom"),sQuery(id+"F54.wireOp",EDGE,"E85.top"),sQuery(id+"F54.wireOp",EDGE,"E85.left"),sQuery(id+"F54.wireOp",EDGE,"E85.right")])],"isStart":false});
            var sketch = newSketch(context, id + "F56", { "sketchPlane" : qUnion([Q0])});
            skLineSegment(sketch, "E86.bottom", {"start": v(4500, 3300) * mm, "end": v(5300, 3300) * mm});
            skLineSegment(sketch, "E86.top", {"start": v(4500, 4440) * mm, "end": v(5300, 4440) * mm});
            skLineSegment(sketch, "E86.left", {"start": v(4500, 3300) * mm, "end": v(4500, 4440) * mm});
            skLineSegment(sketch, "E86.right", {"start": v(5300, 3300) * mm, "end": v(5300, 4440) * mm});
            skSolve(sketch);
        }
        {
            var Q0;
            Q0 = qSketchRegion(id + "F56", true);
            extrude(context, id + "F57", {"entities" : qUnion([Q0]), "operationType" : NewBodyOperationType.ADD, "depth" : 300 * mm, "offsetDistance" : 25 * mm});
        }
        {
            var Q0;
            Q0=makeQuery(id+"F27.opExtrude","CAP_FACE",FACE,{"disambiguationData":[OSD([sQuery(id+"F26.wireOp",EDGE,"E61"),sQuery(id+"F26.wireOp",EDGE,"E62"),sQuery(id+"F26.wireOp",EDGE,"E63"),sQuery(id+"F26.wireOp",EDGE,"E64")])],"isStart":false});
            var sketch = newSketch(context, id + "F58", { "sketchPlane" : qUnion([Q0])});
            skLineSegment(sketch, "E87.bottom", {"start": v(4500, 3300) * mm, "end": v(10500, 3300) * mm});
            skLineSegment(sketch, "E87.top", {"start": v(4500, 2800) * mm, "end": v(10500, 2800) * mm});
            skLineSegment(sketch, "E87.left", {"start": v(4500, 3300) * mm, "end": v(4500, 2800) * mm});
            skLineSegment(sketch, "E87.right", {"start": v(10500, 3300) * mm, "end": v(10500, 2800) * mm});
            skSolve(sketch);
        }
        {
            var Q0;
            Q0 = qSketchRegion(id + "F58", true);
            extrude(context, id + "F59", {"entities" : qUnion([Q0]), "operationType" : NewBodyOperationType.REMOVE, "oppositeDirection" : true, "depth" : 800 * mm, "offsetDistance" : 25 * mm});
        }
        {
            var Q0;
            {var subQ0=sQuery(id+"F20.wireOp",EDGE,"E40");var subQ1=sQuery(id+"F20.wireOp",EDGE,"E39");Q0=makeQuery(id+"F59.boolean.opBoolean","MERGE",FACE,{"derivedFrom":[makeQuery(id+"F47.boolean.opBoolean","MERGE",FACE,{"derivedFrom":[makeQuery(id+"F23.boolean.opBoolean","SPLIT",FACE,{"disambiguationData":[TD([makeQuery(id+"F14.opExtrude","SWEPT_FACE",FACE,{"disambiguationData":[OSD([sQuery(id+"F13.wireOp",EDGE,"E24")])]})])],"derivedFrom":makeQuery(id+"F21.boolean.opBoolean","MERGE",FACE,{"derivedFrom":[makeQuery(id+"F19.boolean.opBoolean","COPY",FACE,{"derivedFrom":makeQuery(id+"F19.opExtrude","CAP_FACE",FACE,{"disambiguationData":[OSD([sQuery(id+"F18.wireOp",EDGE,"E32"),sQuery(id+"F18.wireOp",EDGE,"E33"),sQuery(id+"F18.wireOp",EDGE,"E34"),sQuery(id+"F18.wireOp",EDGE,"E35"),sQuery(id+"F18.wireOp",EDGE,"E36"),sQuery(id+"F18.wireOp",EDGE,"E37")])],"isStart":false})})],"fromTools":[makeQuery(id+"F21.opExtrude","CAP_FACE",FACE,{"disambiguationData":[OSD([sQuery(id+"F20.wireOp",EDGE,"E38"),subQ1,subQ0,sQuery(id+"F20.wireOp",EDGE,"E41")])],"isStart":false})]})}),makeQuery(id+"F47.opExtrude","CAP_FACE",FACE,{"disambiguationData":[OSD([sQuery(id+"F46.wireOp",EDGE,"E81.bottom"),sQuery(id+"F46.wireOp",EDGE,"E81.top"),sQuery(id+"F46.wireOp",EDGE,"E81.left"),sQuery(id+"F46.wireOp",EDGE,"E81.right")])],"isStart":false})]})],"fromTools":[makeQuery(id+"F59.opExtrude","CAP_FACE",FACE,{"disambiguationData":[OSD([sQuery(id+"F58.wireOp",EDGE,"E87.bottom"),sQuery(id+"F58.wireOp",EDGE,"E87.top"),sQuery(id+"F58.wireOp",EDGE,"E87.left"),sQuery(id+"F58.wireOp",EDGE,"E87.right")])],"isStart":false})]});}
            var sketch = newSketch(context, id + "F60", { "sketchPlane" : qUnion([Q0])});
            skPoint(sketch, "E88.oppositeSnap0", {"position": v(8650, 3300) * mm});
            skLineSegment(sketch, "E88.bottom", {"start": v(10500, 3300) * mm, "end": v(8650, 3300) * mm});
            skLineSegment(sketch, "E88.top", {"start": v(10500, 2800) * mm, "end": v(8650, 2800) * mm});
            skLineSegment(sketch, "E88.left", {"start": v(10500, 3300) * mm, "end": v(10500, 2800) * mm});
            skLineSegment(sketch, "E88.right", {"start": v(8650, 3300) * mm, "end": v(8650, 2800) * mm});
            skSolve(sketch);
        }
        {
            var Q0;
            Q0 = qSketchRegion(id + "F60", true);
            extrude(context, id + "F61", {"entities" : qUnion([Q0]), "operationType" : NewBodyOperationType.REMOVE, "oppositeDirection" : true, "depth" : 2100 * mm, "offsetDistance" : 25 * mm});
        }
        {
            var Q0;
            Q0=makeQuery(id+"F61.boolean.opBoolean","MERGE",FACE,{"derivedFrom":[makeQuery(id+"F33.opExtrude","CAP_FACE",FACE,{"disambiguationData":[OSD([sQuery(id+"F32.wireOp",EDGE,"E74.bottom"),sQuery(id+"F32.wireOp",EDGE,"E74.top"),sQuery(id+"F32.wireOp",EDGE,"E74.left"),sQuery(id+"F32.wireOp",EDGE,"E74.right")])],"isStart":false})],"fromTools":[makeQuery(id+"F61.opExtrude","CAP_FACE",FACE,{"disambiguationData":[OSD([sQuery(id+"F60.wireOp",EDGE,"E88.bottom"),sQuery(id+"F60.wireOp",EDGE,"E88.top"),sQuery(id+"F60.wireOp",EDGE,"E88.left"),sQuery(id+"F60.wireOp",EDGE,"E88.right")])],"isStart":false})]});
            var sketch = newSketch(context, id + "F62", { "sketchPlane" : qUnion([Q0])});
            skLineSegment(sketch, "E89.bottom", {"start": v(8900, 3300) * mm, "end": v(10500, 3300) * mm});
            skLineSegment(sketch, "E89.top", {"start": v(8900, 2800) * mm, "end": v(10500, 2800) * mm});
            skLineSegment(sketch, "E89.left", {"start": v(8900, 3300) * mm, "end": v(8900, 2800) * mm});
            skLineSegment(sketch, "E89.right", {"start": v(10500, 3300) * mm, "end": v(10500, 2800) * mm});
            skSolve(sketch);
        }
        {
            var Q0;
            Q0 = qSketchRegion(id + "F62", true);
            extrude(context, id + "F63", {"entities" : qUnion([Q0]), "operationType" : NewBodyOperationType.REMOVE, "oppositeDirection" : true, "depth" : 300 * mm, "offsetDistance" : 25 * mm});
        }
        {
            var Q0;
            Q0=makeQuery(id+"F63.boolean.opBoolean","MERGE",FACE,{"derivedFrom":[makeQuery(id+"F31.opExtrude","CAP_FACE",FACE,{"disambiguationData":[OSD([sQuery(id+"F30.wireOp",EDGE,"E69"),sQuery(id+"F30.wireOp",EDGE,"E70"),sQuery(id+"F30.wireOp",EDGE,"E71"),sQuery(id+"F30.wireOp",EDGE,"E72"),sQuery(id+"F30.wireOp",EDGE,"E73")])],"isStart":false})],"fromTools":[makeQuery(id+"F63.opExtrude","CAP_FACE",FACE,{"disambiguationData":[OSD([sQuery(id+"F62.wireOp",EDGE,"E89.bottom"),sQuery(id+"F62.wireOp",EDGE,"E89.top"),sQuery(id+"F62.wireOp",EDGE,"E89.left"),sQuery(id+"F62.wireOp",EDGE,"E89.right")])],"isStart":false})]});
            var sketch = newSketch(context, id + "F64", { "sketchPlane" : qUnion([Q0])});
            skLineSegment(sketch, "E90.bottom", {"start": v(9200, 3300) * mm, "end": v(10500, 3300) * mm});
            skLineSegment(sketch, "E90.top", {"start": v(9200, 2800) * mm, "end": v(10500, 2800) * mm});
            skLineSegment(sketch, "E90.left", {"start": v(9200, 3300) * mm, "end": v(9200, 2800) * mm});
            skLineSegment(sketch, "E90.right", {"start": v(10500, 3300) * mm, "end": v(10500, 2800) * mm});
            skSolve(sketch);
        }
        {
            var Q0;
            Q0 = qSketchRegion(id + "F64", true);
            extrude(context, id + "F65", {"entities" : qUnion([Q0]), "operationType" : NewBodyOperationType.REMOVE, "oppositeDirection" : true, "depth" : 300 * mm, "offsetDistance" : 25 * mm});
        }
        {
            var Q0;
            Q0=makeQuery(id+"F65.boolean.opBoolean","MERGE",FACE,{"derivedFrom":[makeQuery(id+"F29.opExtrude","CAP_FACE",FACE,{"disambiguationData":[OSD([sQuery(id+"F28.wireOp",EDGE,"E65"),sQuery(id+"F28.wireOp",EDGE,"E66"),sQuery(id+"F28.wireOp",EDGE,"E67"),sQuery(id+"F28.wireOp",EDGE,"E68")])],"isStart":false})],"fromTools":[makeQuery(id+"F65.opExtrude","CAP_FACE",FACE,{"disambiguationData":[OSD([sQuery(id+"F64.wireOp",EDGE,"E90.bottom"),sQuery(id+"F64.wireOp",EDGE,"E90.top"),sQuery(id+"F64.wireOp",EDGE,"E90.left"),sQuery(id+"F64.wireOp",EDGE,"E90.right")])],"isStart":false})]});
            var sketch = newSketch(context, id + "F66", { "sketchPlane" : qUnion([Q0])});
            skLineSegment(sketch, "E91.bottom", {"start": v(9500, 3300) * mm, "end": v(10500, 3300) * mm});
            skLineSegment(sketch, "E91.top", {"start": v(9500, 2800) * mm, "end": v(10500, 2800) * mm});
            skLineSegment(sketch, "E91.left", {"start": v(9500, 3300) * mm, "end": v(9500, 2800) * mm});
            skLineSegment(sketch, "E91.right", {"start": v(10500, 3300) * mm, "end": v(10500, 2800) * mm});
            skSolve(sketch);
        }
        {
            var Q0;
            Q0 = qSketchRegion(id + "F66", true);
            extrude(context, id + "F67", {"entities" : qUnion([Q0]), "operationType" : NewBodyOperationType.REMOVE, "oppositeDirection" : true, "depth" : 300 * mm, "offsetDistance" : 25 * mm});
        }
        {
            var Q0;
            {var subQ1=sQuery(id+"F22.wireOp",EDGE,"E50");Q0=makeQuery(id+"F25.boolean.opBoolean","SPLIT",FACE,{"disambiguationData":[TD([makeQuery(id+"F14.opExtrude","SWEPT_FACE",FACE,{"disambiguationData":[OSD([sQuery(id+"F13.wireOp",EDGE,"E24")])]})])],"derivedFrom":makeQuery(id+"F23.boolean.opBoolean","COPY",FACE,{"derivedFrom":makeQuery(id+"F23.opExtrude","CAP_FACE",FACE,{"disambiguationData":[OSD([sQuery(id+"F22.wireOp",EDGE,"E42"),sQuery(id+"F22.wireOp",EDGE,"E43"),sQuery(id+"F22.wireOp",EDGE,"E44"),sQuery(id+"F22.wireOp",EDGE,"E45"),sQuery(id+"F22.wireOp",EDGE,"E46"),sQuery(id+"F22.wireOp",EDGE,"E47"),sQuery(id+"F22.wireOp",EDGE,"E48"),sQuery(id+"F22.wireOp",EDGE,"E49"),subQ1,sQuery(id+"F22.wireOp",EDGE,"E51")])],"isStart":false})})});}
            var sketch = newSketch(context, id + "F68", { "sketchPlane" : qUnion([Q0])});
            skLineSegment(sketch, "E92", {"start": v(4500, -3700) * mm, "end": v(4500, -4870) * mm});
            skLineSegment(sketch, "E93", {"start": v(4500, -4870) * mm, "end": v(-14089.93, -4870) * mm});
            skLineSegment(sketch, "E94", {"start": v(-14089.93, -4870) * mm, "end": v(-14089.93, -3700) * mm});
            skLineSegment(sketch, "E95", {"start": v(-14089.93, -3700) * mm, "end": v(4196.76, -3700) * mm});
            skLineSegment(sketch, "E96", {"start": v(4196.76, -3700) * mm, "end": v(4500, -3700) * mm});
            skSolve(sketch);
        }
        {
            var Q0;
            Q0 = qSketchRegion(id + "F68", true);
            extrude(context, id + "F69", {"entities" : qUnion([Q0]), "operationType" : NewBodyOperationType.ADD, "depth" : 3000 * mm, "offsetDistance" : 25 * mm});
        }
        {
            var Q0;
            Q0=makeQuery(id+"F67.boolean.opBoolean","MERGE",FACE,{"derivedFrom":[makeQuery(id+"F25.boolean.opBoolean","COPY",FACE,{"derivedFrom":makeQuery(id+"F25.opExtrude","CAP_FACE",FACE,{"disambiguationData":[OSD([sQuery(id+"F24.wireOp",EDGE,"E52"),sQuery(id+"F24.wireOp",EDGE,"E53"),sQuery(id+"F24.wireOp",EDGE,"E54"),sQuery(id+"F24.wireOp",EDGE,"E55"),sQuery(id+"F24.wireOp",EDGE,"E56"),sQuery(id+"F24.wireOp",EDGE,"E57"),sQuery(id+"F24.wireOp",EDGE,"E58"),sQuery(id+"F24.wireOp",EDGE,"E59"),sQuery(id+"F24.wireOp",EDGE,"E60")])],"isStart":false})})],"fromTools":[makeQuery(id+"F67.opExtrude","CAP_FACE",FACE,{"disambiguationData":[OSD([sQuery(id+"F66.wireOp",EDGE,"E91.bottom"),sQuery(id+"F66.wireOp",EDGE,"E91.top"),sQuery(id+"F66.wireOp",EDGE,"E91.left"),sQuery(id+"F66.wireOp",EDGE,"E91.right")])],"isStart":false})]});
            var sketch = newSketch(context, id + "F70", { "sketchPlane" : qUnion([Q0])});
            skLineSegment(sketch, "E97", {"start": v(-11279.87, -5700) * mm, "end": v(-11279.87, -6870) * mm});
            skLineSegment(sketch, "E98", {"start": v(-11279.87, -6870) * mm, "end": v(4500, -6870) * mm});
            skLineSegment(sketch, "E99", {"start": v(4500, -6870) * mm, "end": v(4500, -5700) * mm});
            skLineSegment(sketch, "E100", {"start": v(4500, -5700) * mm, "end": v(-11279.87, -5700) * mm});
            skSolve(sketch);
        }
        {
            var Q0;
            Q0 = qSketchRegion(id + "F70", true);
            extrude(context, id + "F71", {"entities" : qUnion([Q0]), "operationType" : NewBodyOperationType.ADD, "depth" : 1500 * mm, "offsetDistance" : 25 * mm});
        }
        {
            var Q0;
            Q0=makeQuery(id+"F23.boolean.opBoolean","SPLIT",FACE,{"disambiguationData":[TD([makeQuery(id+"F14.opExtrude","SWEPT_FACE",FACE,{"disambiguationData":[OSD([sQuery(id+"F13.wireOp",EDGE,"E26")])]})])],"derivedFrom":makeQuery(id+"F21.boolean.opBoolean","MERGE",FACE,{"derivedFrom":[makeQuery(id+"F19.boolean.opBoolean","COPY",FACE,{"derivedFrom":makeQuery(id+"F19.opExtrude","CAP_FACE",FACE,{"disambiguationData":[OSD([sQuery(id+"F18.wireOp",EDGE,"E32"),sQuery(id+"F18.wireOp",EDGE,"E33"),sQuery(id+"F18.wireOp",EDGE,"E34"),sQuery(id+"F18.wireOp",EDGE,"E35"),sQuery(id+"F18.wireOp",EDGE,"E36"),sQuery(id+"F18.wireOp",EDGE,"E37")])],"isStart":false})})],"fromTools":[makeQuery(id+"F21.opExtrude","CAP_FACE",FACE,{"disambiguationData":[OSD([sQuery(id+"F20.wireOp",EDGE,"E38"),sQuery(id+"F20.wireOp",EDGE,"E39"),sQuery(id+"F20.wireOp",EDGE,"E40"),sQuery(id+"F20.wireOp",EDGE,"E41")])],"isStart":false})]})});
            var sketch = newSketch(context, id + "F72", { "sketchPlane" : qUnion([Q0])});
            skLineSegment(sketch, "E101", {"start": v(-14089.93, -3700) * mm, "end": v(-14089.93, -4870) * mm});
            skLineSegment(sketch, "E102", {"start": v(-14089.93, -4870) * mm, "end": v(-16900, -4870) * mm});
            skLineSegment(sketch, "E103", {"start": v(-16900, -4870) * mm, "end": v(-16900, -3700) * mm});
            skLineSegment(sketch, "E104", {"start": v(-16900, -3700) * mm, "end": v(-14089.93, -3700) * mm});
            skSolve(sketch);
        }
        {
            var Q0;
            Q0 = qSketchRegion(id + "F72", true);
            extrude(context, id + "F73", {"entities" : qUnion([Q0]), "operationType" : NewBodyOperationType.ADD, "depth" : 1500 * mm, "offsetDistance" : 25 * mm});
        }
    });
